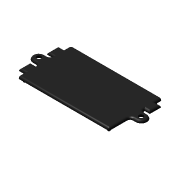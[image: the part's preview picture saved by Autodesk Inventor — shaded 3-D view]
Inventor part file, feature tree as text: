
AUTODESK INVENTOR PART (.ipt)
format: ipt  version: 2012 (Build 160160000, 160)  size: 278,016 bytes
history: native  units: mm
features: extrude x4, sketch x4, fillet x3, other x1
ambient origin geometry x8: Origin, YZ Plane, XZ Plane, XY Plane, X Axis, Y Axis, Z Axis, Center Point
feature tree (12):
  other  "Твердое тело1"
  extrude  "Выдавливание1"  Depth=65.0mm
  extrude  "Выдавливание2"  Depth=65.0mm
  extrude  "Выдавливание3"  Depth=4.0mm
  extrude  "Выдавливание4"  Depth=38.0mm
  fillet  "Сопряжение3"  Radius=8.0mm
  fillet  "Сопряжение4"  Radius=2.0mm
  fillet  "Сопряжение5"  Radius=2.0mm
  sketch  "Эскиз1"
  sketch  "Эскиз2"
  sketch  "Эскиз3"
  sketch  "Эскиз5"
